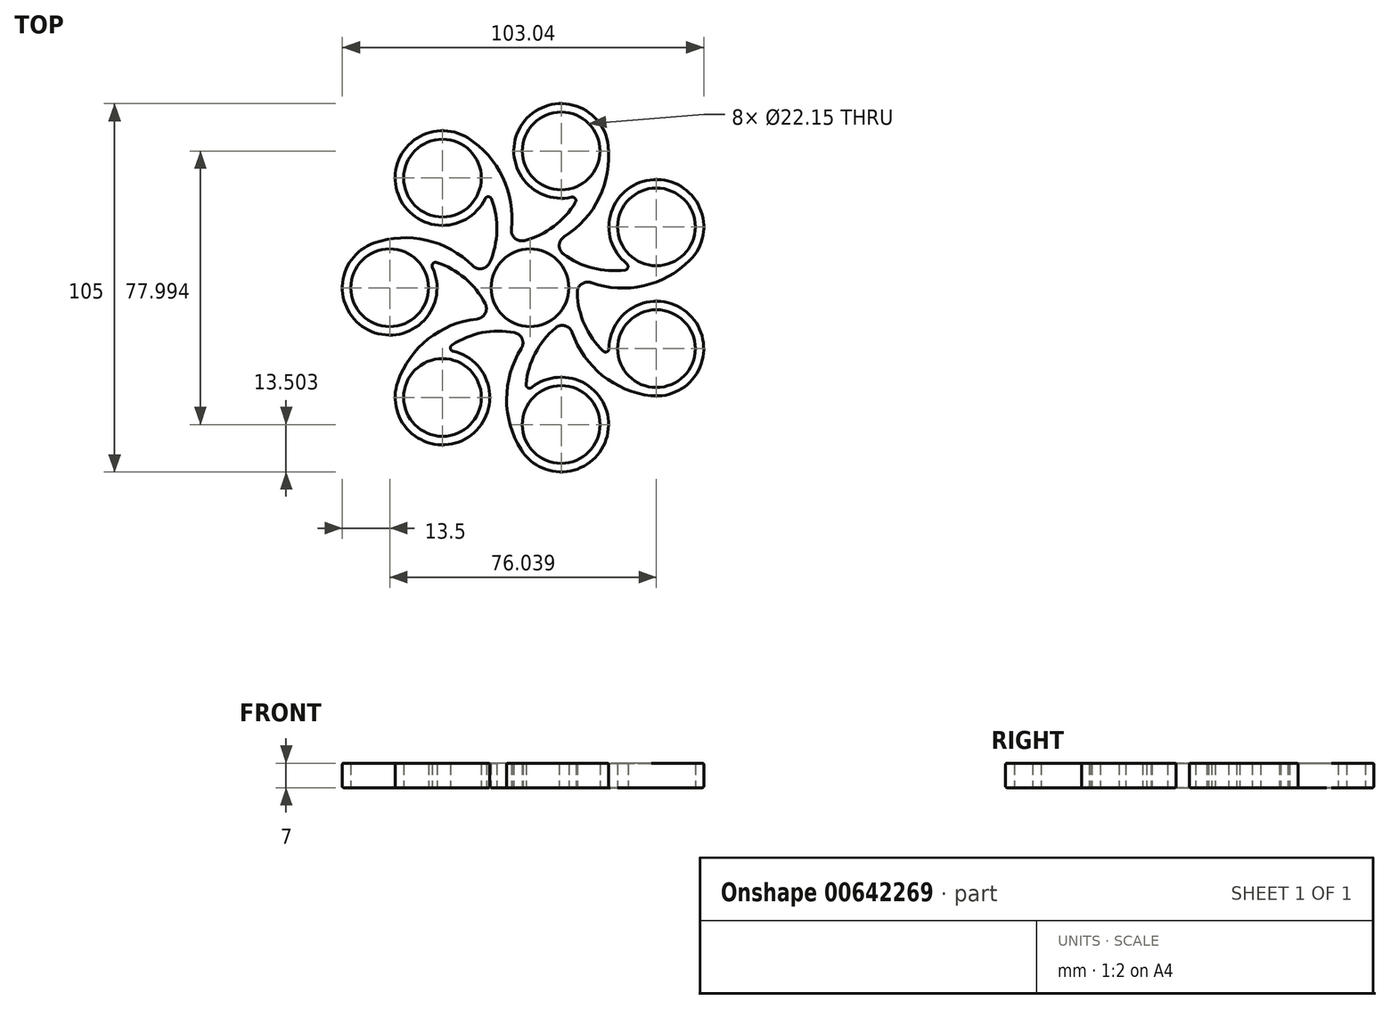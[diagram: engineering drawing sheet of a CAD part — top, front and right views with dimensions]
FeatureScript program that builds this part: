
annotation { "Feature Type Name" : "Feature", "Feature Type Description" : "" }
export const myFeature = defineFeature(function(context is Context, id is Id, definition is map)
    precondition{}
    {
        {
            var Q0;
            Q0=qCreatedBy(makeId("Top.planeOp"),FACE);
            var sketch = newSketch(context, id + "F0", { "sketchPlane" : qUnion([Q0])});
            skCircle(sketch, "E0", {"center": v(0, 0) * mm, "radius": 11.07 * mm});
            skCircle(sketch, "E1", {"center": v(0, 0) * mm, "radius": 13.5 * mm});
            skLineSegment(sketch, "E2", {"start": v(0, 0) * mm, "end": v(-40, 0) * mm, "construction": true});
            skCircle(sketch, "E3", {"center": v(-40, 0) * mm, "radius": 11.07 * mm});
            skCircle(sketch, "E4", {"center": v(-40, 0) * mm, "radius": 13.5 * mm});
            skLineSegment(sketch, "E5", {"start": v(-40, 0) * mm, "end": v(-40, -13.5) * mm, "construction": true});
            skLineSegment(sketch, "E6", {"start": v(0, 0) * mm, "end": v(0, 13.5) * mm, "construction": true});
            skLineSegment(sketch, "E7", {"start": v(-40, 0) * mm, "end": v(-30.45, -9.55) * mm, "construction": true});
            skLineSegment(sketch, "E8", {"start": v(0, 0) * mm, "end": v(-9.55, 9.55) * mm});
            skLineSegment(sketch, "E9", {"start": v(0, 0) * mm, "end": v(0, -13.5) * mm, "construction": true});
            skLineSegment(sketch, "E10", {"start": v(0, 0) * mm, "end": v(-9.55, -9.55) * mm, "construction": true});
            skArc(sketch, "E11.trimOffspring", {"start": v(-12.6, -4.86) * mm, "mid": v(-19.36, 3.37) * mm, "end": v(-29.02, 7.86) * mm});
            skArc(sketch, "E12.trimOffspring", {"start": v(-13.26, 2.52) * mm, "mid": v(-27.13, 12.92) * mm, "end": v(-44.46, 12.74) * mm});
            skArc(sketch, "E13.1.0", {"start": v(-4.05, -12.88) * mm, "mid": v(-14.7, -13.04) * mm, "end": v(-24.24, -17.8) * mm});
            skCircle(sketch, "E13.1.1", {"center": v(-24.94, -31.27) * mm, "radius": 13.5 * mm});
            skArc(sketch, "E13.1.2", {"start": v(-10.24, -8.8) * mm, "mid": v(-27.01, -13.16) * mm, "end": v(-37.68, -26.82) * mm});
            skLineSegment(sketch, "E13.1.3", {"start": v(-24.94, -31.27) * mm, "end": v(-14.38, -39.7) * mm, "construction": true});
            skCircle(sketch, "E13.1.4", {"center": v(-24.94, -31.27) * mm, "radius": 11.07 * mm});
            skLineSegment(sketch, "E13.1.5", {"start": v(-24.94, -31.27) * mm, "end": v(-11.52, -29.76) * mm, "construction": true});
            skArc(sketch, "E13.2.0", {"start": v(7.54, -11.2) * mm, "mid": v(1.03, -19.63) * mm, "end": v(-1.2, -30.04) * mm});
            skCircle(sketch, "E13.2.1", {"center": v(8.9, -39) * mm, "radius": 13.5 * mm});
            skArc(sketch, "E13.2.2", {"start": v(0.5, -13.5) * mm, "mid": v(-6.55, -29.32) * mm, "end": v(-2.53, -46.18) * mm});
            skLineSegment(sketch, "E13.2.3", {"start": v(8.9, -39) * mm, "end": v(22.06, -36) * mm, "construction": true});
            skCircle(sketch, "E13.2.4", {"center": v(8.9, -39) * mm, "radius": 11.07 * mm});
            skLineSegment(sketch, "E13.2.5", {"start": v(8.9, -39) * mm, "end": v(16.08, -27.57) * mm, "construction": true});
            skArc(sketch, "E13.3.0", {"start": v(13.46, -1.09) * mm, "mid": v(15.98, -11.44) * mm, "end": v(22.74, -19.67) * mm});
            skCircle(sketch, "E13.3.1", {"center": v(36.04, -17.36) * mm, "radius": 13.5 * mm});
            skArc(sketch, "E13.3.2", {"start": v(10.86, -8.02) * mm, "mid": v(18.84, -23.4) * mm, "end": v(34.53, -30.77) * mm});
            skLineSegment(sketch, "E13.3.3", {"start": v(36.04, -17.36) * mm, "end": v(41.9, -5.2) * mm, "construction": true});
            skCircle(sketch, "E13.3.4", {"center": v(36.04, -17.36) * mm, "radius": 11.07 * mm});
            skLineSegment(sketch, "E13.3.5", {"start": v(36.04, -17.36) * mm, "end": v(31.58, -4.61) * mm, "construction": true});
            skArc(sketch, "E13.4.0", {"start": v(9.24, 9.84) * mm, "mid": v(18.9, 5.37) * mm, "end": v(29.56, 5.51) * mm});
            skCircle(sketch, "E13.4.1", {"center": v(36.04, 17.36) * mm, "radius": 13.5 * mm});
            skArc(sketch, "E13.4.2", {"start": v(13.04, 3.49) * mm, "mid": v(30.05, 0.13) * mm, "end": v(45.59, 7.81) * mm});
            skLineSegment(sketch, "E13.4.3", {"start": v(36.04, 17.36) * mm, "end": v(30.18, 29.52) * mm, "construction": true});
            skCircle(sketch, "E13.4.4", {"center": v(36.04, 17.36) * mm, "radius": 11.07 * mm});
            skLineSegment(sketch, "E13.4.5", {"start": v(36.04, 17.36) * mm, "end": v(23.3, 21.81) * mm, "construction": true});
            skArc(sketch, "E14.1.5.0", {"start": v(-1.93, 13.36) * mm, "mid": v(7.6, 18.13) * mm, "end": v(14.12, 26.55) * mm});
            skCircle(sketch, "E14.4.5.0", {"center": v(8.9, 39) * mm, "radius": 13.5 * mm});
            skArc(sketch, "E14.6.5.0", {"start": v(5.4, 12.37) * mm, "mid": v(18.63, 23.58) * mm, "end": v(22.32, 40.51) * mm});
            skLineSegment(sketch, "E14.10.5.0", {"start": v(8.9, 39) * mm, "end": v(-4.26, 42) * mm, "construction": true});
            skCircle(sketch, "E14.13.5.0", {"center": v(8.9, 39) * mm, "radius": 11.07 * mm});
            skLineSegment(sketch, "E14.15.5.0", {"start": v(8.9, 39) * mm, "end": v(-2.53, 31.81) * mm, "construction": true});
            skArc(sketch, "E15.1.6.0", {"start": v(-11.65, 6.82) * mm, "mid": v(-9.44, 17.24) * mm, "end": v(-11.95, 27.59) * mm});
            skCircle(sketch, "E15.4.6.0", {"center": v(-24.94, 31.27) * mm, "radius": 13.5 * mm});
            skArc(sketch, "E15.6.6.0", {"start": v(-6.3, 11.94) * mm, "mid": v(-6.82, 29.26) * mm, "end": v(-17.76, 42.7) * mm});
            skLineSegment(sketch, "E15.10.6.0", {"start": v(-24.94, 31.27) * mm, "end": v(-35.5, 22.86) * mm, "construction": true});
            skCircle(sketch, "E15.13.6.0", {"center": v(-24.94, 31.27) * mm, "radius": 11.07 * mm});
            skLineSegment(sketch, "E15.15.6.0", {"start": v(-24.94, 31.27) * mm, "end": v(-26.45, 17.86) * mm, "construction": true});
            skSolve(sketch);
        }
        {
            var Q0;
            Q0=makeQuery(id+"F0.imprint","IMPRINT",FACE,{"disambiguationData":[TD([[makeQuery(id+"F0.imprint","IMPRINT",EDGE,{"derivedFrom":sQuery(id+"F0.wireOp",EDGE,"E0")}),-1.0]])]});
            var Q1;
            {var subQ0=sQuery(id+"F0.wireOp",EDGE,"E11.trimOffspring");Q1=makeQuery(id+"F0.imprint","IMPRINT",FACE,{"disambiguationData":[TD([[makeQuery(id+"F0.imprint","IMPRINT",EDGE,{"derivedFrom":subQ0}),-1.0]])]});}
            var Q2;
            {var subQ1=sQuery(id+"F0.wireOp",EDGE,"E15.1.6.0");Q2=makeQuery(id+"F0.imprint","IMPRINT",FACE,{"disambiguationData":[TD([[makeQuery(id+"F0.imprint","IMPRINT",EDGE,{"derivedFrom":subQ1}),-1.0]])]});}
            var Q3;
            {var subQ0=sQuery(id+"F0.wireOp",EDGE,"E14.1.5.0");Q3=makeQuery(id+"F0.imprint","IMPRINT",FACE,{"disambiguationData":[TD([[makeQuery(id+"F0.imprint","IMPRINT",EDGE,{"derivedFrom":subQ0}),-1.0]])]});}
            var Q4;
            {var subQ0=sQuery(id+"F0.wireOp",EDGE,"E13.4.0");Q4=makeQuery(id+"F0.imprint","IMPRINT",FACE,{"disambiguationData":[TD([[makeQuery(id+"F0.imprint","IMPRINT",EDGE,{"derivedFrom":subQ0}),-1.0]])]});}
            var Q5;
            {var subQ0=sQuery(id+"F0.wireOp",EDGE,"E13.3.0");Q5=makeQuery(id+"F0.imprint","IMPRINT",FACE,{"disambiguationData":[TD([[makeQuery(id+"F0.imprint","IMPRINT",EDGE,{"derivedFrom":subQ0}),-1.0]])]});}
            var Q6;
            {var subQ0=sQuery(id+"F0.wireOp",EDGE,"E13.2.0");Q6=makeQuery(id+"F0.imprint","IMPRINT",FACE,{"disambiguationData":[TD([[makeQuery(id+"F0.imprint","IMPRINT",EDGE,{"derivedFrom":subQ0}),-1.0]])]});}
            var Q7;
            {var subQ0=sQuery(id+"F0.wireOp",EDGE,"E13.1.0");Q7=makeQuery(id+"F0.imprint","IMPRINT",FACE,{"disambiguationData":[TD([[makeQuery(id+"F0.imprint","IMPRINT",EDGE,{"derivedFrom":subQ0}),-1.0]])]});}
            var Q8;
            Q8=makeQuery(id+"F0.imprint","IMPRINT",FACE,{"disambiguationData":[TD([[makeQuery(id+"F0.imprint","IMPRINT",EDGE,{"derivedFrom":sQuery(id+"F0.wireOp",EDGE,"E13.1.4")}),-1.0]])]});
            var Q9;
            Q9=makeQuery(id+"F0.imprint","IMPRINT",FACE,{"disambiguationData":[TD([[makeQuery(id+"F0.imprint","IMPRINT",EDGE,{"derivedFrom":sQuery(id+"F0.wireOp",EDGE,"E3")}),-1.0]])]});
            var Q10;
            Q10=makeQuery(id+"F0.imprint","IMPRINT",FACE,{"disambiguationData":[TD([[makeQuery(id+"F0.imprint","IMPRINT",EDGE,{"derivedFrom":sQuery(id+"F0.wireOp",EDGE,"E15.13.6.0")}),-1.0]])]});
            var Q11;
            Q11=makeQuery(id+"F0.imprint","IMPRINT",FACE,{"disambiguationData":[TD([[makeQuery(id+"F0.imprint","IMPRINT",EDGE,{"derivedFrom":sQuery(id+"F0.wireOp",EDGE,"E14.13.5.0")}),-1.0]])]});
            var Q12;
            Q12=makeQuery(id+"F0.imprint","IMPRINT",FACE,{"disambiguationData":[TD([[makeQuery(id+"F0.imprint","IMPRINT",EDGE,{"derivedFrom":sQuery(id+"F0.wireOp",EDGE,"E13.4.4")}),-1.0]])]});
            var Q13;
            Q13=makeQuery(id+"F0.imprint","IMPRINT",FACE,{"disambiguationData":[TD([[makeQuery(id+"F0.imprint","IMPRINT",EDGE,{"derivedFrom":sQuery(id+"F0.wireOp",EDGE,"E13.3.4")}),-1.0]])]});
            var Q14;
            Q14=makeQuery(id+"F0.imprint","IMPRINT",FACE,{"disambiguationData":[TD([[makeQuery(id+"F0.imprint","IMPRINT",EDGE,{"derivedFrom":sQuery(id+"F0.wireOp",EDGE,"E13.2.4")}),-1.0]])]});
            extrude(context, id + "F1", {"entities" : qUnion([Q0, Q1, Q2, Q3, Q4, Q5, Q6, Q7, Q8, Q9, Q10, Q11, Q12, Q13, Q14]), "depth" : 7 * mm, "offsetDistance" : 25 * mm});
        }
        {
            var Q0;
            Q0=makeQuery(id+"F1.opExtrude","SWEPT_EDGE",EDGE,{"disambiguationData":[OSD([sQuery(id+"F0.wireOp",EDGE,"E4"),sQuery(id+"F0.wireOp",EDGE,"E11.trimOffspring")])]});
            var Q1;
            Q1=makeQuery(id+"F1.opExtrude","SWEPT_EDGE",EDGE,{"disambiguationData":[OSD([sQuery(id+"F0.wireOp",EDGE,"E15.1.6.0"),sQuery(id+"F0.wireOp",EDGE,"E15.4.6.0")])]});
            var Q2;
            Q2=makeQuery(id+"F1.opExtrude","SWEPT_EDGE",EDGE,{"disambiguationData":[OSD([sQuery(id+"F0.wireOp",EDGE,"E14.1.5.0"),sQuery(id+"F0.wireOp",EDGE,"E14.4.5.0")])]});
            var Q3;
            Q3=makeQuery(id+"F1.opExtrude","SWEPT_EDGE",EDGE,{"disambiguationData":[OSD([sQuery(id+"F0.wireOp",EDGE,"E13.4.0"),sQuery(id+"F0.wireOp",EDGE,"E13.4.1")])]});
            var Q4;
            Q4=makeQuery(id+"F1.opExtrude","SWEPT_EDGE",EDGE,{"disambiguationData":[OSD([sQuery(id+"F0.wireOp",EDGE,"E13.3.0"),sQuery(id+"F0.wireOp",EDGE,"E13.3.1")])]});
            var Q5;
            Q5=makeQuery(id+"F1.opExtrude","SWEPT_EDGE",EDGE,{"disambiguationData":[OSD([sQuery(id+"F0.wireOp",EDGE,"E13.1.0"),sQuery(id+"F0.wireOp",EDGE,"E13.1.1")])]});
            var Q6;
            Q6=makeQuery(id+"F1.opExtrude","SWEPT_EDGE",EDGE,{"disambiguationData":[OSD([sQuery(id+"F0.wireOp",EDGE,"E13.2.0"),sQuery(id+"F0.wireOp",EDGE,"E13.2.1")])]});
            fillet(context, id + "F2", {"entities" : qUnion([Q0, Q1, Q2, Q3, Q4, Q5, Q6]), "radius" : 1 * mm, "tangentPropagation" : true, "allowEdgeOverflow" : false});
        }
        {
            var Q0;
            Q0=makeQuery(id+"F1.opExtrude","SWEPT_EDGE",EDGE,{"disambiguationData":[OSD([sQuery(id+"F0.wireOp",EDGE,"E1"),sQuery(id+"F0.wireOp",EDGE,"E12.trimOffspring")])]});
            var Q1;
            Q1=makeQuery(id+"F1.opExtrude","SWEPT_EDGE",EDGE,{"disambiguationData":[OSD([sQuery(id+"F0.wireOp",EDGE,"E1"),sQuery(id+"F0.wireOp",EDGE,"E15.6.6.0")])]});
            var Q2;
            Q2=makeQuery(id+"F1.opExtrude","SWEPT_EDGE",EDGE,{"disambiguationData":[OSD([sQuery(id+"F0.wireOp",EDGE,"E1"),sQuery(id+"F0.wireOp",EDGE,"E14.6.5.0")])]});
            var Q3;
            Q3=makeQuery(id+"F1.opExtrude","SWEPT_EDGE",EDGE,{"disambiguationData":[OSD([sQuery(id+"F0.wireOp",EDGE,"E1"),sQuery(id+"F0.wireOp",EDGE,"E13.4.2")])]});
            var Q4;
            Q4=makeQuery(id+"F1.opExtrude","SWEPT_EDGE",EDGE,{"disambiguationData":[OSD([sQuery(id+"F0.wireOp",EDGE,"E1"),sQuery(id+"F0.wireOp",EDGE,"E13.3.2")])]});
            var Q5;
            Q5=makeQuery(id+"F1.opExtrude","SWEPT_EDGE",EDGE,{"disambiguationData":[OSD([sQuery(id+"F0.wireOp",EDGE,"E1"),sQuery(id+"F0.wireOp",EDGE,"E13.1.2")])]});
            var Q6;
            Q6=makeQuery(id+"F1.opExtrude","SWEPT_EDGE",EDGE,{"disambiguationData":[OSD([sQuery(id+"F0.wireOp",EDGE,"E1"),sQuery(id+"F0.wireOp",EDGE,"E13.2.2")])]});
            fillet(context, id + "F3", {"entities" : qUnion([Q0, Q1, Q2, Q3, Q4, Q5, Q6]), "radius" : 3 * mm, "tangentPropagation" : true, "allowEdgeOverflow" : false});
        }
        {
            var Q0;
            Q0=makeQuery(id+"F1.opExtrude","CAP_FACE",FACE,{"disambiguationData":[OSD([sQuery(id+"F0.wireOp",EDGE,"E0"),sQuery(id+"F0.wireOp",EDGE,"E1"),sQuery(id+"F0.wireOp",EDGE,"E3"),sQuery(id+"F0.wireOp",EDGE,"E4"),sQuery(id+"F0.wireOp",EDGE,"E11.trimOffspring"),sQuery(id+"F0.wireOp",EDGE,"E12.trimOffspring"),sQuery(id+"F0.wireOp",EDGE,"E13.1.0"),sQuery(id+"F0.wireOp",EDGE,"E13.1.1"),sQuery(id+"F0.wireOp",EDGE,"E13.1.2"),sQuery(id+"F0.wireOp",EDGE,"E13.1.4"),sQuery(id+"F0.wireOp",EDGE,"E13.2.0"),sQuery(id+"F0.wireOp",EDGE,"E13.2.1"),sQuery(id+"F0.wireOp",EDGE,"E13.2.2"),sQuery(id+"F0.wireOp",EDGE,"E13.2.4"),sQuery(id+"F0.wireOp",EDGE,"E13.3.0"),sQuery(id+"F0.wireOp",EDGE,"E13.3.1"),sQuery(id+"F0.wireOp",EDGE,"E13.3.2"),sQuery(id+"F0.wireOp",EDGE,"E13.3.4"),sQuery(id+"F0.wireOp",EDGE,"E13.4.0"),sQuery(id+"F0.wireOp",EDGE,"E13.4.1"),sQuery(id+"F0.wireOp",EDGE,"E13.4.2"),sQuery(id+"F0.wireOp",EDGE,"E13.4.4")])],"isStart":false});
            var Q1;
            Q1=makeQuery(id+"F1.opExtrude","CAP_EDGE",EDGE,{"disambiguationData":[OSD([sQuery(id+"F0.wireOp",EDGE,"E13.1.1")])],"isStart":true});
            fillet(context, id + "F4", {"entities" : qUnion([Q0, Q1]), "radius" : .4 * mm, "tangentPropagation" : true, "allowEdgeOverflow" : false});
        }
    });
